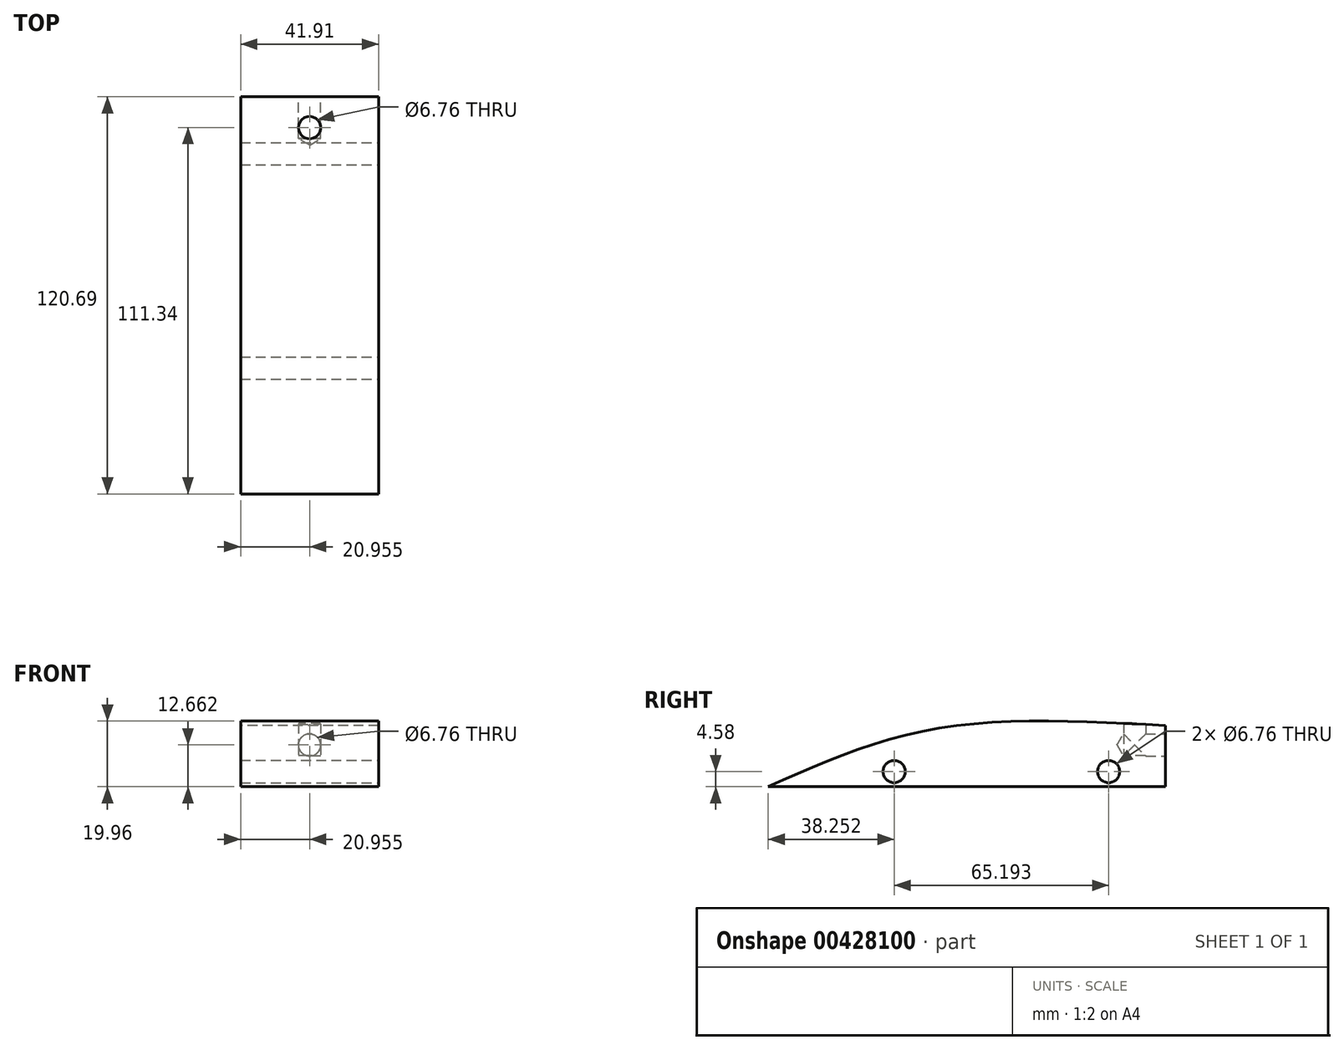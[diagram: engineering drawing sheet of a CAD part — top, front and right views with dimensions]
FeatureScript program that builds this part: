
annotation { "Feature Type Name" : "Feature", "Feature Type Description" : "" }
export const myFeature = defineFeature(function(context is Context, id is Id, definition is map)
    precondition{}
    {
        {
            var Q0;
            Q0=qCreatedBy(makeId("Right.planeOp"),FACE);
            var sketch = newSketch(context, id + "F0", { "sketchPlane" : qUnion([Q0])});
            skLineSegment(sketch, "E0", {"start": v(-61.15, 0) * mm, "end": v(59.54, 0) * mm});
            skFitSpline(sketch, "E1", {"points": [v(-61.15, 0) * mm, v(-10.78, 17.51) * mm, v(59.54, 18.59) * mm], "startDerivative": vector(102.8, 45.9) * mm, "endDerivative": vector(137.78, -7.5) * mm});
            skLineSegment(sketch, "E2", {"start": v(59.54, 18.59) * mm, "end": v(59.54, 0) * mm});
            skPoint(sketch, "E3", {"position": v(-21.28, 3.5) * mm});
            skPoint(sketch, "E4", {"position": v(43.1, 3.5) * mm});
            skSolve(sketch);
        }
        {
            var Q0;
            Q0 = qSketchRegion(id + "F0", true);
            extrude(context, id + "F1", {"entities" : qUnion([Q0]), "depth" : 41.9 * mm});
        }
        {
            var Q0;
            Q0=makeQuery(id+"F1.opExtrude","CAP_FACE",FACE,{"disambiguationData":[OSD([sQuery(id+"F0.wireOp",EDGE,"E0"),sQuery(id+"F0.wireOp",EDGE,"E1"),sQuery(id+"F0.wireOp",EDGE,"E2")])],"isStart":false});
            var sketch = newSketch(context, id + "F2", { "sketchPlane" : qUnion([Q0])});
            skCircle(sketch, "E5", {"center": v(-22.9, 4.58) * mm, "radius": 3.01 * mm});
            skCircle(sketch, "E6", {"center": v(42.3, 4.58) * mm, "radius": 3.01 * mm});
            skSolve(sketch);
        }
        {
            var Q0;
            Q0=sQuery(id+"F2.wireOp",VERTEX,"E5.center");
            var Q1;
            Q1=sQuery(id+"F2.wireOp",VERTEX,"E6.center");
            var Q2;
            Q2=makeQuery(id+"F1.opExtrude","SWEPT_BODY",BODY,{"disambiguationData":[OSD([sQuery(id+"F0.wireOp",EDGE,"E0"),sQuery(id+"F0.wireOp",EDGE,"E1"),sQuery(id+"F0.wireOp",EDGE,"E2")])]});
            hole(context, id + "F3", {"style" : HoleStyle.SIMPLE, "endStyle" : HoleEndStyle.THROUGH, "standardTappedOrClearance" : lookupTablePath({ "standard" : "ANSI", "fit" : "Normal (ASME)", "size" : "1/4", "type" : "Clearance" }), "standardBlindInLast" : lookupTablePath({ "fit" : "Free", "standard" : "ANSI", "size" : "1/4", "type" : "Clearance" }), "holeDiameter" : 6.76 * mm, "isTappedThrough" : true, "tappedDepth" : 12.7 * mm, "tapClearance" : 3, "startFromSketch" : true, "locations" : qUnion([Q0, Q1]), "scope" : qUnion([Q2])});
        }
        {
            var Q0;
            Q0=makeQuery(id+"F1.opExtrude","SWEPT_FACE",FACE,{"disambiguationData":[OSD([sQuery(id+"F0.wireOp",EDGE,"E2")])]});
            var sketch = newSketch(context, id + "F4", { "sketchPlane" : qUnion([Q0])});
            skCircle(sketch, "E7", {"center": v(-20.96, 12.66) * mm, "radius": 2.7 * mm});
            skPoint(sketch, "E7.centerSnap0", {"position": v(-20.96, 18.59) * mm});
            skSolve(sketch);
        }
        {
            var Q0;
            Q0=sQuery(id+"F4.wireOp",VERTEX,"E7.center");
            var Q1;
            Q1=makeQuery(id+"F1.opExtrude","SWEPT_BODY",BODY,{"disambiguationData":[OSD([sQuery(id+"F0.wireOp",EDGE,"E0"),sQuery(id+"F0.wireOp",EDGE,"E1"),sQuery(id+"F0.wireOp",EDGE,"E2")])]});
            hole(context, id + "F5", {"style" : HoleStyle.SIMPLE, "endStyle" : HoleEndStyle.BLIND, "holeDiameter" : 6.76 * mm, "holeDepth" : 12.7 * mm, "isTappedThrough" : true, "tappedDepth" : 12.7 * mm, "tapClearance" : 3, "startFromSketch" : true, "locations" : qUnion([Q0]), "scope" : qUnion([Q1])});
        }
        {
            var Q0;
            Q0=makeQuery(id+"F1.opExtrude","SWEPT_FACE",FACE,{"disambiguationData":[OSD([sQuery(id+"F0.wireOp",EDGE,"E0")])]});
            var sketch = newSketch(context, id + "F6", { "sketchPlane" : qUnion([Q0])});
            skCircle(sketch, "E8", {"center": v(20.96, -50.19) * mm, "radius": 3.53 * mm});
            skPoint(sketch, "E8.centerSnap0", {"position": v(20.96, -59.54) * mm});
            skSolve(sketch);
        }
        {
            var Q0;
            Q0=sQuery(id+"F6.wireOp",VERTEX,"E8.center");
            var Q1;
            Q1=makeQuery(id+"F1.opExtrude","SWEPT_BODY",BODY,{"disambiguationData":[OSD([sQuery(id+"F0.wireOp",EDGE,"E0"),sQuery(id+"F0.wireOp",EDGE,"E1"),sQuery(id+"F0.wireOp",EDGE,"E2")])]});
            hole(context, id + "F7", {"style" : HoleStyle.SIMPLE, "endStyle" : HoleEndStyle.THROUGH, "holeDiameter" : 6.76 * mm, "isTappedThrough" : true, "tappedDepth" : 12.7 * mm, "tapClearance" : 3, "startFromSketch" : true, "locations" : qUnion([Q0]), "scope" : qUnion([Q1])});
        }
        {
            var Q0;
            Q0=makeQuery(id+"F1.opExtrude","SWEPT_FACE",FACE,{"disambiguationData":[OSD([sQuery(id+"F0.wireOp",EDGE,"E0")])]});
            var sketch = newSketch(context, id + "F8", { "sketchPlane" : qUnion([Q0])});
            skCircle(sketch, "E9", {"center": v(20.96, -50.19) * mm, "radius": 3.48 * mm});
            skSolve(sketch);
        }
        {
            var Q0;
            Q0 = qSketchRegion(id + "F8", true);
            extrude(context, id + "F9", {"entities" : qUnion([Q0]), "operationType" : NewBodyOperationType.ADD, "oppositeDirection" : true, "depth" : 9.4 * mm});
        }
    });
